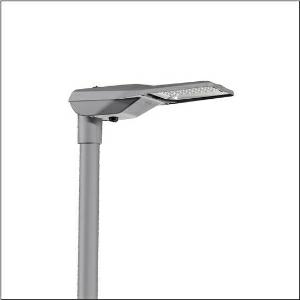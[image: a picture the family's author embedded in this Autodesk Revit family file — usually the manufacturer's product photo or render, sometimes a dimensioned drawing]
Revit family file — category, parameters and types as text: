
# Revit family: streetlight_sl_21_mini___st1_0ab_5xe2m33t08gb_59c5
name_source: partatom
category: Lighting Fixtures
units: mm (PartAtom-declared; Revit-internal decimal feet)

## family parameters
Cut with Voids When Loaded = No
Host = Face
Light Source = No
Part Type = Normal
Room Calculation Point = No
Round Connector Dimension = Use Diameter
Shared = No

## types (1)
- --- (1 x LED, 5230 lm, 40.4 W, 3000K)
    Apparent Load = 40 VA
    CIE Flux Codes = 38 73 97 100 100
    Color Rendering = 70
    Color Temperature = 3000K
    Default Elevation = 1800 mm
    Description = Streetlight SL 21 mini, mast luminaire, primary light control with lens, of PMMA, primary optical cover: cover, of toughened safety glass, transparent, light distribution: ST1.0aB, light emission: direct distribution, primary light characteristic: asymmetric, installation type: side-entry, post-top, LED, High Power LED, rated luminous flux: 5.230lm, luminous efficacy: 130lm/W, light colour: 730, colour temperature: 3000K, control gear: D4i, control: flexible luminous flux parameterisation, time-dependent luminous flux control, constant luminous flux control, overheat protection, pre-setting: logarithmic dimming characteristic, mains connection: 220..240V, AC, 50/60Hz, start of lifetime: 40W, end of service life: 41W, reduction: 19W, luminaire housing, of diecast aluminium, powder-coated, Siteco® metallic grey (DB 702S), corrosivity category C5 mid according to DIN EN ISO 12944, please order mast flange separately, inclination adjustable: 0°, 5°, 10°, 15°, sealing non-destructively replaceable, multi-level sealing system, length: 628mm, width: 235mm, height: 110mm, mast flange for spigot size: 42mm (side-entry): 5XC10008XM4, 60/48mm (side-entry/post-top): 5XC10108XM2, 76/60mm (side-entry/post-top): 5XC10108XM1, mounting height: 4..8m, Smart Interface below and above, protection rating (complete): IP66, insulation class (complete): insulation class II (safety insulation), certification: CE, ENEC, ENEC+, VDE, impact resistance: IK10, permissible operating ambient temperature for outdoor applications: -40..+50°C, standard-compliant lighting for roads and squares, packaging unit: 1 piece

Light Distribution: ST1.0aB
    Height = 110 mm
    Lamp = 1 x LED
    Lamp Light Flux = 5230 lm
    Lamp Power = 40.4 W
    Lamp count = 1
    Length = 625 mm
    Luminous efficacy = 129 lm/W
    Manufacturer = Siteco
    ModVariant = No
    Model = 5XE2M33T08GB
    Number of Poles = 1
    OnlyDefault = Yes
    Power Factor = 1
    Product Name = Streetlight SL 21 mini | ST1.0aB
    Product group = mast luminaire | pylon top
    ProductGroupID = 6100
    Protection Class = Protection class II
    Protection Degree = IP 66
    RLX_Detail_Level = 1
    RLX_Emergency_Light_Flux = 0 lm
    RLX_Emergency_Type = 0
    RLX_Emergency_Type_DB = No
    RlxData = <blob elided: 26369 chars, md5=4f4660d4>
    Socket = socket
    Standby Power = 0 W
    System Light Flux = 5230 lm
    System Power = 40 W
    Type Comments = factory setting: luminous flux: 100 % | dim-lin: 254 | 812 mA
    Type Image = l_1003514.jpg
    URL = http://relux.com
    VarID = @adj_203843
    Voltage = 0 V
    Weight = 0.00 kg
    Width = 234 mm

## geometry (parser evidence)
native form markers: Blend x4, Sweep x12
no freeform markers — native parametric forms only
